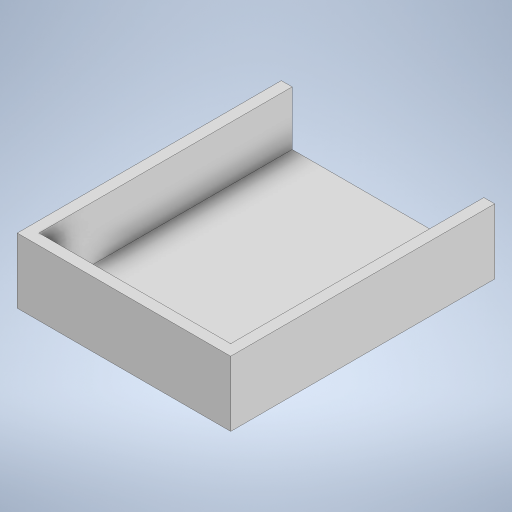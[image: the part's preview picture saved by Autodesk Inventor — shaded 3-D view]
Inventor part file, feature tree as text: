
AUTODESK INVENTOR PART (.ipt)
format: ipt  version: 2023 (Build 270158000, 158)  size: 232,960 bytes
history: native  units: in
note: dims shown in document units (in); Inventor stores cm internally (conversion verified against a paired STEP export)
features: sketch x3, extrude x2, shell x1
ambient origin geometry x8: Origin, YZ Plane, XZ Plane, XY Plane, X Axis, Y Axis, Z Axis, Center Point
bodies: Solid1 (feature_tree)
feature tree (6):
  extrude  "Extrusion1"  Depth=2.874in
  shell  "Shell1"  Thickness=0.7087in
  sketch  "Sketch4"  dims[d4=0.1181in d17=0.3937in d18=0.0in]
  extrude  "Extrusion3"  Depth=0.1181in TaperAngle=0.0deg
  sketch  "Sketch2"  dims[d0=2.3228in d1=2.874in d2=0.7087in d3=0.0in]
  sketch  "Sketch5"  dims[d13=0.0197in d14=0.0344in d15=0.0197in d16=0.0344in d19=0.0197in d20=0.0344in]
